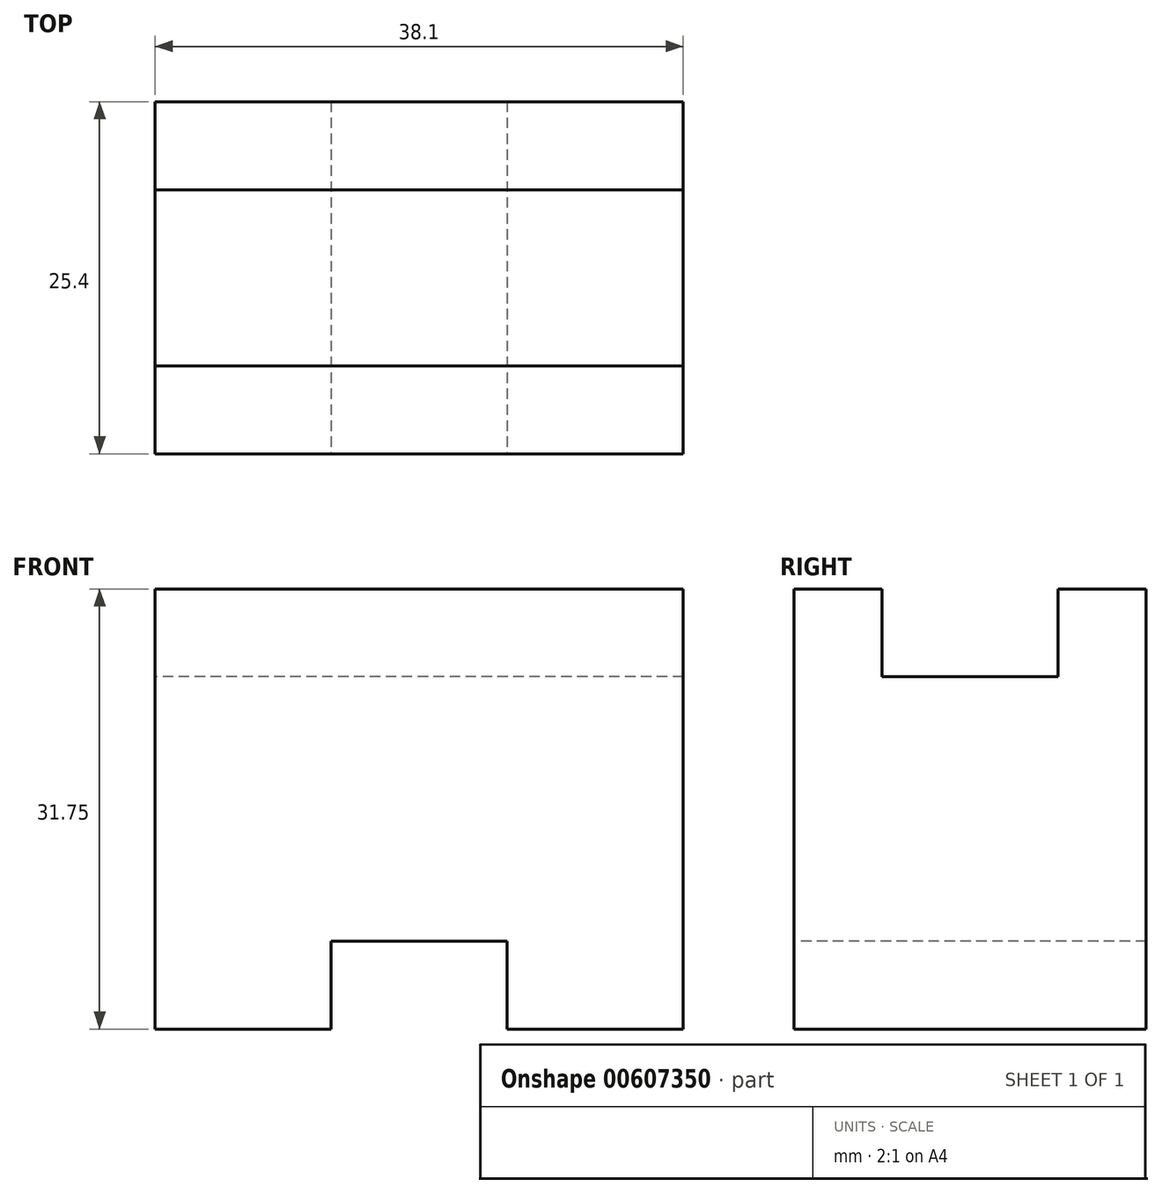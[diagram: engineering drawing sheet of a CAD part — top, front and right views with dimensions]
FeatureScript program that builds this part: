
annotation { "Feature Type Name" : "Feature", "Feature Type Description" : "" }
export const myFeature = defineFeature(function(context is Context, id is Id, definition is map)
    precondition{}
    {
        {
            var Q0;
            Q0=qCreatedBy(makeId("Right.planeOp"),FACE);
            var sketch = newSketch(context, id + "F0", { "sketchPlane" : qUnion([Q0])});
            skLineSegment(sketch, "E0", {"start": v(0, 0) * mm, "end": v(0, 31.75) * mm});
            skLineSegment(sketch, "E1", {"start": v(0, 31.75) * mm, "end": v(25.4, 31.75) * mm});
            skLineSegment(sketch, "E2", {"start": v(25.4, 31.75) * mm, "end": v(25.4, 0) * mm});
            skLineSegment(sketch, "E3", {"start": v(25.4, 0) * mm, "end": v(0, 0) * mm});
            skLineSegment(sketch, "E4", {"start": v(25.4, 31.75) * mm, "end": v(19.05, 31.75) * mm});
            skLineSegment(sketch, "E5", {"start": v(19.05, 31.75) * mm, "end": v(19.05, 25.4) * mm});
            skLineSegment(sketch, "E6", {"start": v(19.05, 25.4) * mm, "end": v(6.35, 25.4) * mm});
            skLineSegment(sketch, "E7", {"start": v(6.35, 25.4) * mm, "end": v(6.35, 31.75) * mm});
            skLineSegment(sketch, "E8", {"start": v(6.35, 31.75) * mm, "end": v(0, 31.75) * mm});
            skSolve(sketch);
        }
        {
            var Q0;
            Q0=makeQuery(id+"F0.imprint","IMPRINT",FACE,{"disambiguationData":[TD([[makeQuery(id+"F0.imprint","IMPRINT",EDGE,{"derivedFrom":sQuery(id+"F0.wireOp",EDGE,"E0")}),-1.0]])]});
            extrude(context, id + "F1", {"entities" : qUnion([Q0]), "depth" : 38.1 * mm, "offsetDistance" : 25.4 * mm});
        }
        {
            var Q0;
            Q0=makeQuery(id+"F1.opExtrude","SWEPT_FACE",FACE,{"disambiguationData":[OSD([sQuery(id+"F0.wireOp",EDGE,"E0")])]});
            var sketch = newSketch(context, id + "F2", { "sketchPlane" : qUnion([Q0])});
            skLineSegment(sketch, "E9", {"start": v(0, 0) * mm, "end": v(12.7, 0) * mm});
            skLineSegment(sketch, "E10", {"start": v(12.7, 0) * mm, "end": v(12.7, 6.35) * mm});
            skLineSegment(sketch, "E11", {"start": v(12.7, 6.35) * mm, "end": v(25.4, 6.35) * mm});
            skLineSegment(sketch, "E12", {"start": v(25.4, 6.35) * mm, "end": v(25.4, 0) * mm});
            skLineSegment(sketch, "E13", {"start": v(25.4, 0) * mm, "end": v(38.1, 0) * mm});
            skLineSegment(sketch, "E14", {"start": v(38.1, 0) * mm, "end": v(12.7, 0) * mm});
            skSolve(sketch);
        }
        {
            var Q0;
            {var subQ0=sQuery(id+"F2.wireOp",EDGE,"E10");Q0=makeQuery(id+"F2.imprint","IMPRINT",FACE,{"disambiguationData":[TD([[makeQuery(id+"F2.imprint","IMPRINT",EDGE,{"derivedFrom":subQ0}),-1.0]])]});}
            extrude(context, id + "F3", {"entities" : qUnion([Q0]), "operationType" : NewBodyOperationType.REMOVE, "oppositeDirection" : true, "depth" : 25.4 * mm, "offsetDistance" : 25.4 * mm});
        }
    });
